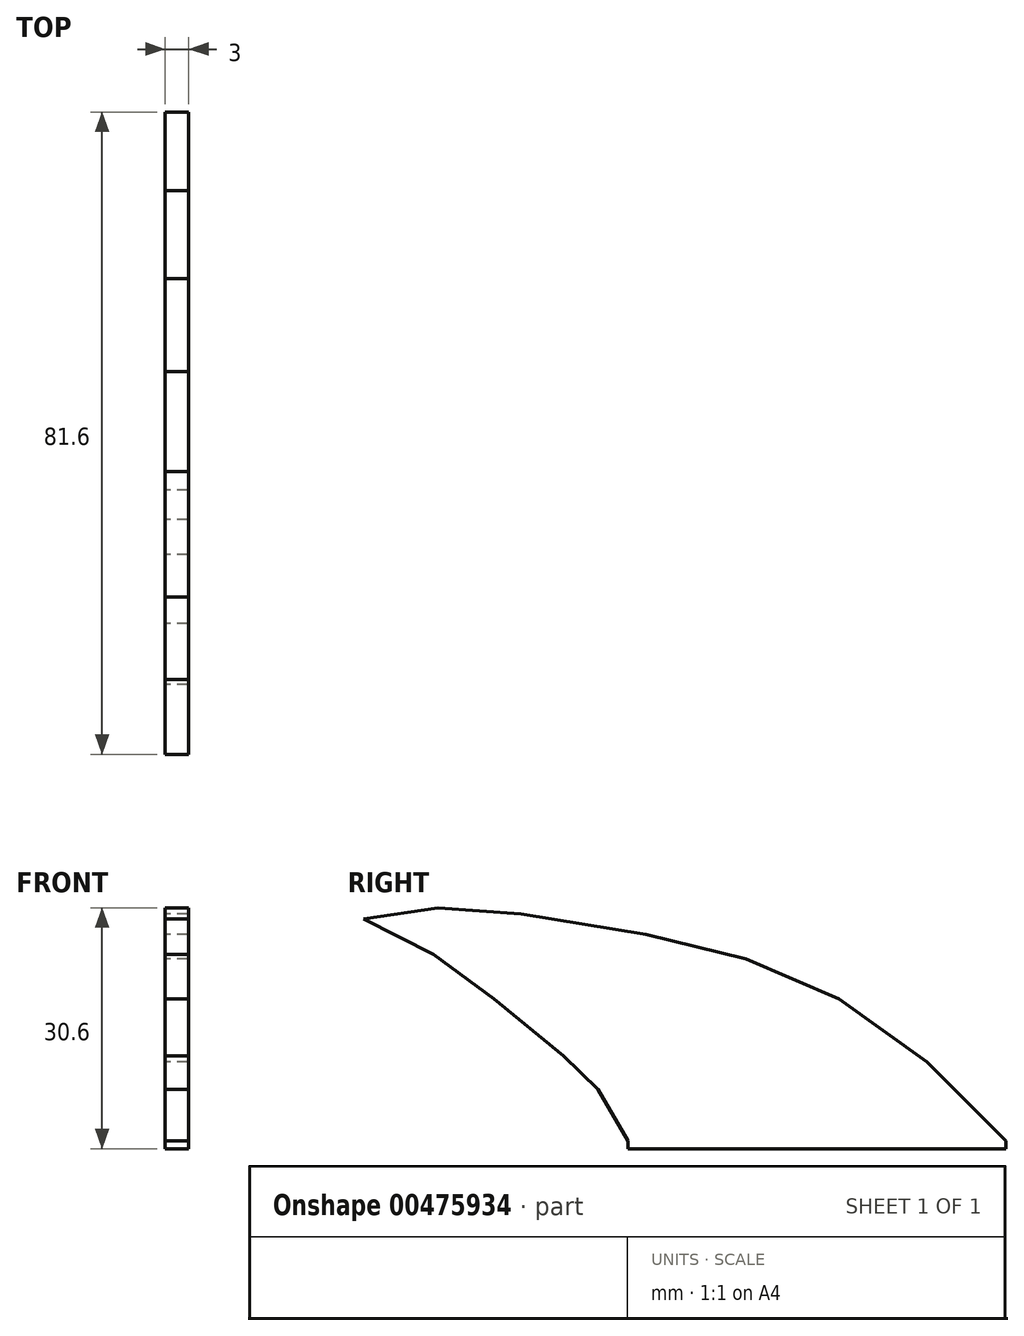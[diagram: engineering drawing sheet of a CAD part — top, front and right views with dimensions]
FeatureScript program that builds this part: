
annotation { "Feature Type Name" : "Feature", "Feature Type Description" : "" }
export const myFeature = defineFeature(function(context is Context, id is Id, definition is map)
    precondition{}
    {
        {
            var Q0;
            Q0=qCreatedBy(makeId("Right.planeOp"),FACE);
            var sketch = newSketch(context, id + "F0", { "sketchPlane" : qUnion([Q0])});
            skLineSegment(sketch, "E0.top", {"start": v(21.23, -0.68) * mm, "end": v(-26.77, -0.68) * mm});
            skLineSegment(sketch, "E1", {"start": v(0.03, 17.32) * mm, "end": v(11.23, 9.32) * mm});
            skLineSegment(sketch, "E2", {"start": v(21.23, -0.68) * mm, "end": v(11.23, 9.32) * mm});
            skLineSegment(sketch, "E3", {"start": v(-11.77, 22.42) * mm, "end": v(0.03, 17.32) * mm});
            skLineSegment(sketch, "E4", {"start": v(-24.47, 25.52) * mm, "end": v(-11.77, 22.42) * mm});
            skLineSegment(sketch, "E5", {"start": v(-40.37, 28.12) * mm, "end": v(-24.47, 25.52) * mm});
            skLineSegment(sketch, "E6", {"start": v(-50.87, 28.92) * mm, "end": v(-40.37, 28.12) * mm});
            skLineSegment(sketch, "E7", {"start": v(-60.37, 27.52) * mm, "end": v(-50.87, 28.92) * mm});
            skLineSegment(sketch, "E8", {"start": v(-30.57, 5.88) * mm, "end": v(-26.77, -0.68) * mm});
            skLineSegment(sketch, "E9", {"start": v(-34.97, 10.12) * mm, "end": v(-30.57, 5.88) * mm});
            skLineSegment(sketch, "E10", {"start": v(-43.77, 17.32) * mm, "end": v(-34.97, 10.12) * mm});
            skPoint(sketch, "E11.endSnap0", {"position": v(-6.87, -0.68) * mm});
            skLineSegment(sketch, "E12", {"start": v(-51.47, 23.02) * mm, "end": v(-43.77, 17.32) * mm});
            skLineSegment(sketch, "E13", {"start": v(-51.47, 23.02) * mm, "end": v(-60.37, 27.52) * mm});
            skLineSegment(sketch, "E14.top", {"start": v(21.23, -1.68) * mm, "end": v(-26.77, -1.68) * mm});
            skLineSegment(sketch, "E14.left", {"start": v(21.23, -0.68) * mm, "end": v(21.23, -1.68) * mm});
            skLineSegment(sketch, "E14.right", {"start": v(-26.77, -0.68) * mm, "end": v(-26.77, -1.68) * mm});
            skSolve(sketch);
        }
        {
            var Q0;
            Q0 = qSketchRegion(id + "F0", true);
            extrude(context, id + "F1", {"entities" : qUnion([Q0]), "endBound" : BoundingType.SYMMETRIC, "depth" : 3 * mm, "offsetDistance" : 25 * mm});
        }
    });
